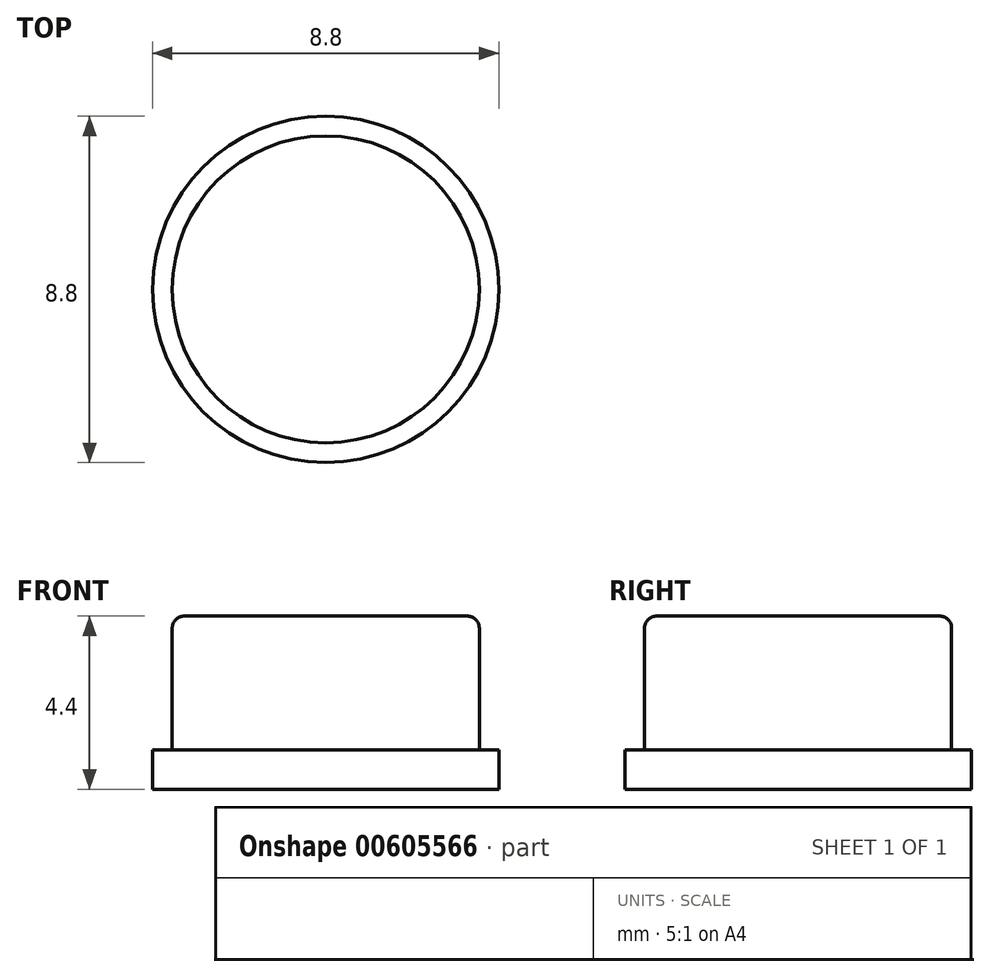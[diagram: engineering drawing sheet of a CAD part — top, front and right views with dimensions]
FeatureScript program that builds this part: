
annotation { "Feature Type Name" : "Feature", "Feature Type Description" : "" }
export const myFeature = defineFeature(function(context is Context, id is Id, definition is map)
    precondition{}
    {
        {
            var Q0;
            Q0=qCreatedBy(makeId("Top.planeOp"),FACE);
            var sketch = newSketch(context, id + "F0", { "sketchPlane" : qUnion([Q0])});
            skCircle(sketch, "E0", {"center": v(-17.63, 7) * mm, "radius": 3.9 * mm});
            skPoint(sketch, "E0.centerSnap0", {"position": v(-20.63, 7) * mm});
            skPoint(sketch, "E0.centerSnap1", {"position": v(-17.63, 4) * mm});
            skCircle(sketch, "E1", {"center": v(-17.63, 7) * mm, "radius": 4.4 * mm});
            skSolve(sketch);
        }
        {
            var Q0;
            Q0=makeQuery(id+"F0.imprint","IMPRINT",FACE,{"disambiguationData":[TD([[makeQuery(id+"F0.imprint","IMPRINT",EDGE,{"derivedFrom":sQuery(id+"F0.wireOp",EDGE,"E0")}),-1.0]])]});
            var Q1;
            Q1=makeQuery(id+"F0.imprint","IMPRINT",FACE,{"disambiguationData":[TD([[makeQuery(id+"F0.imprint","IMPRINT",EDGE,{"derivedFrom":sQuery(id+"F0.wireOp",EDGE,"E0")}),1.0]])]});
            var Q2;
            Q2=makeQuery(id+"F0.imprint","IMPRINT",FACE,{"disambiguationData":[TD([[makeQuery(id+"F0.imprint","IMPRINT",EDGE,{"derivedFrom":sQuery(id+"F0.wireOp",EDGE,"25a58777-480c-44bc-9d97-0f3e8529d1bb")}),1.0]])]});
            var Q3;
            Q3=makeQuery(id+"F0.imprint","IMPRINT",FACE,{"disambiguationData":[TD([[makeQuery(id+"F0.imprint","IMPRINT",EDGE,{"derivedFrom":sQuery(id+"F0.wireOp",EDGE,"25a58777-480c-44bc-9d97-0f3e8529d1bb")}),-1.0]])]});
            extrude(context, id + "F1", {"entities" : qUnion([Q0, Q1, Q2, Q3]), "depth" : 1 * mm, "offsetDistance" : 25 * mm});
        }
        {
            var Q0;
            Q0=makeQuery(id+"F0.imprint","IMPRINT",FACE,{"disambiguationData":[TD([[makeQuery(id+"F0.imprint","IMPRINT",EDGE,{"derivedFrom":sQuery(id+"F0.wireOp",EDGE,"25a58777-480c-44bc-9d97-0f3e8529d1bb")}),1.0]])]});
            var Q1;
            Q1=makeQuery(id+"F0.imprint","IMPRINT",FACE,{"disambiguationData":[TD([[makeQuery(id+"F0.imprint","IMPRINT",EDGE,{"derivedFrom":sQuery(id+"F0.wireOp",EDGE,"E0")}),1.0]])]});
            extrude(context, id + "F2", {"entities" : qUnion([Q0, Q1]), "operationType" : NewBodyOperationType.ADD, "depth" : 4.4 * mm, "offsetDistance" : 25 * mm});
        }
        {
            var Q0;
            Q0=makeQuery(id+"F2.opExtrude","CAP_EDGE",EDGE,{"disambiguationData":[OSD([sQuery(id+"F0.wireOp",EDGE,"E0")])],"isStart":false});
            var Q1;
            Q1=makeQuery(id+"F2.opExtrude","CAP_EDGE",EDGE,{"disambiguationData":[OSD([sQuery(id+"F0.wireOp",EDGE,"25a58777-480c-44bc-9d97-0f3e8529d1bb")])],"isStart":false});
            fillet(context, id + "F3", {"entities" : qUnion([Q0, Q1]), "radius" : .3 * mm, "tangentPropagation" : true, "allowEdgeOverflow" : false});
        }
    });
